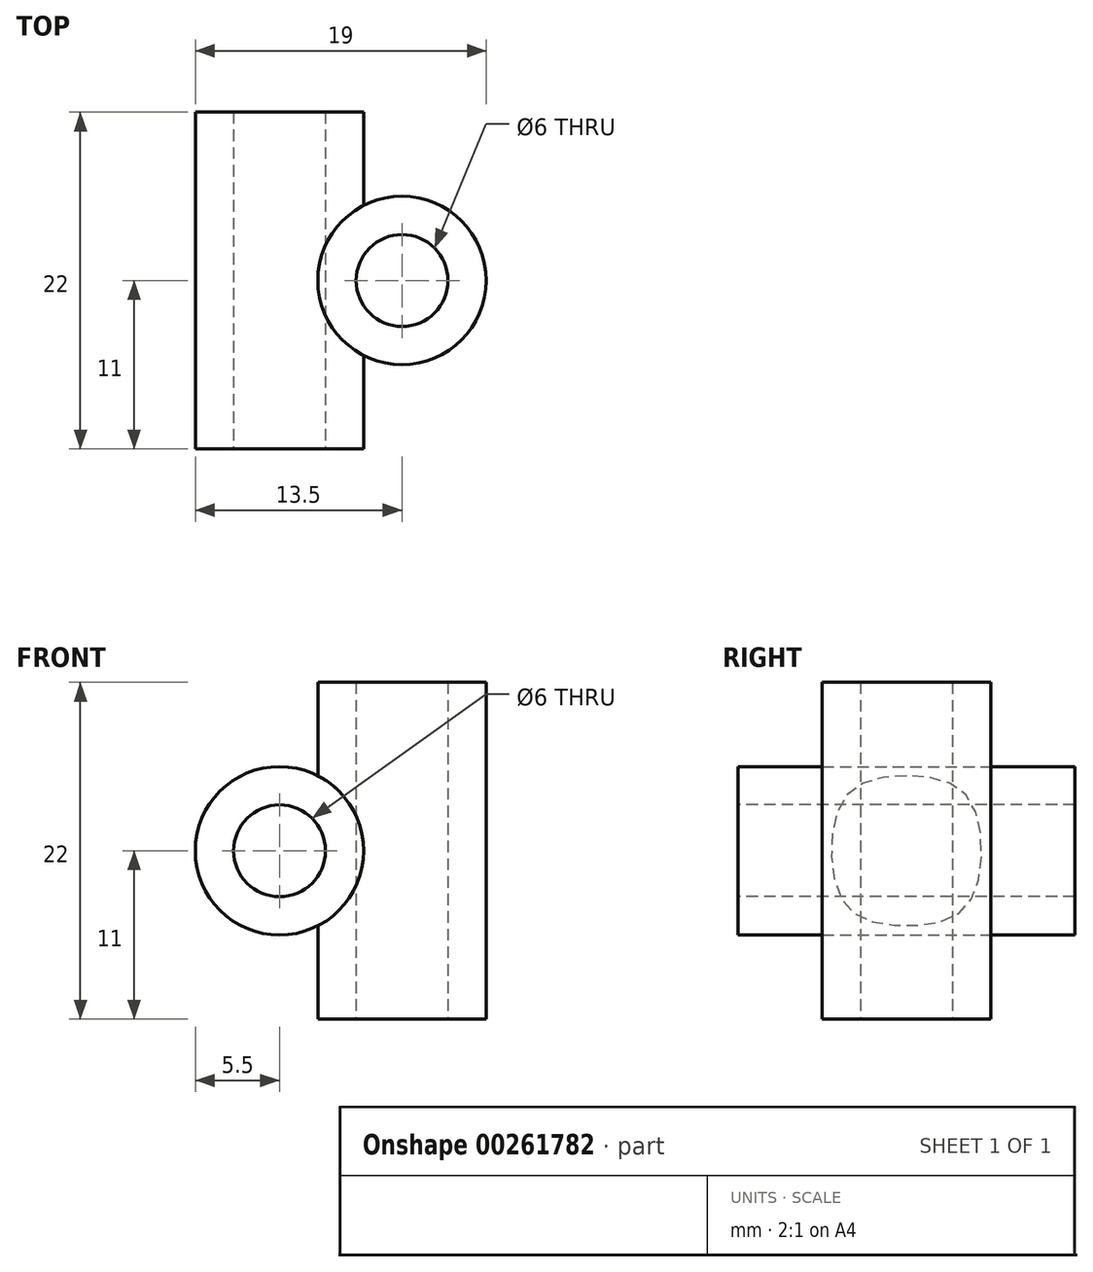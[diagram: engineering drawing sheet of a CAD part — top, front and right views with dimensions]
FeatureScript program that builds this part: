
annotation { "Feature Type Name" : "Feature", "Feature Type Description" : "" }
export const myFeature = defineFeature(function(context is Context, id is Id, definition is map)
    precondition{}
    {
        {
            var Q0;
            Q0=qCreatedBy(makeId("Front.planeOp"),FACE);
            var sketch = newSketch(context, id + "F0", { "sketchPlane" : qUnion([Q0])});
            skCircle(sketch, "E0", {"center": v(0, 0) * mm, "radius": 5.5 * mm});
            skCircle(sketch, "E1", {"center": v(0, 0) * mm, "radius": 3 * mm});
            skSolve(sketch);
        }
        {
            var Q0;
            Q0=makeQuery(id+"F0.imprint","IMPRINT",FACE,{"disambiguationData":[TD([[makeQuery(id+"F0.imprint","IMPRINT",EDGE,{"derivedFrom":sQuery(id+"F0.wireOp",EDGE,"E1")}),1.0]])]});
            var Q1;
            Q1=makeQuery(id+"F0.imprint","IMPRINT",FACE,{"disambiguationData":[TD([[makeQuery(id+"F0.imprint","IMPRINT",EDGE,{"derivedFrom":sQuery(id+"F0.wireOp",EDGE,"E0")}),1.0]])]});
            extrude(context, id + "F1", {"entities" : qUnion([Q0, Q1]), "endBound" : BoundingType.SYMMETRIC, "depth" : 22 * mm});
        }
        {
            var Q0;
            Q0=qCreatedBy(makeId("Top.planeOp"),FACE);
            var sketch = newSketch(context, id + "F2", { "sketchPlane" : qUnion([Q0])});
            skCircle(sketch, "E2", {"center": v(8, 0) * mm, "radius": 5.5 * mm});
            skCircle(sketch, "E3", {"center": v(8, 0) * mm, "radius": 3 * mm});
            skSolve(sketch);
        }
        {
            var Q0;
            Q0=makeQuery(id+"F2.imprint","IMPRINT",FACE,{"disambiguationData":[TD([[makeQuery(id+"F2.imprint","IMPRINT",EDGE,{"derivedFrom":sQuery(id+"F2.wireOp",EDGE,"E3")}),1.0]])]});
            var Q1;
            Q1=makeQuery(id+"F2.imprint","IMPRINT",FACE,{"disambiguationData":[TD([[makeQuery(id+"F2.imprint","IMPRINT",EDGE,{"derivedFrom":sQuery(id+"F2.wireOp",EDGE,"E2")}),1.0]])]});
            extrude(context, id + "F3", {"entities" : qUnion([Q0, Q1]), "operationType" : NewBodyOperationType.ADD, "endBound" : BoundingType.SYMMETRIC, "depth" : 22 * mm});
        }
        {
            var Q0;
            Q0=qCreatedBy(makeId("Front.planeOp"),FACE);
            var sketch = newSketch(context, id + "F4", { "sketchPlane" : qUnion([Q0])});
            skCircle(sketch, "E4.0", {"center": v(0, 0) * mm, "radius": 3 * mm});
            skSolve(sketch);
        }
        {
            var Q0;
            Q0 = qSketchRegion(id + "F4", true);
            extrude(context, id + "F5", {"entities" : qUnion([Q0]), "operationType" : NewBodyOperationType.REMOVE, "endBound" : BoundingType.SYMMETRIC, "oppositeDirection" : true, "depth" : 25 * mm});
        }
        {
            var Q0;
            Q0=makeQuery(id+"F3.opExtrude","CAP_FACE",FACE,{"disambiguationData":[OSD([sQuery(id+"F2.wireOp",EDGE,"E2")])],"isStart":true});
            var sketch = newSketch(context, id + "F6", { "sketchPlane" : qUnion([Q0])});
            skCircle(sketch, "E5.0", {"center": v(8, 0) * mm, "radius": 3 * mm});
            skSolve(sketch);
        }
        {
            var Q0;
            Q0 = qSketchRegion(id + "F6", true);
            extrude(context, id + "F7", {"entities" : qUnion([Q0]), "operationType" : NewBodyOperationType.REMOVE, "endBound" : BoundingType.THROUGH_ALL, "oppositeDirection" : true, "depth" : 25 * mm});
        }
    });
